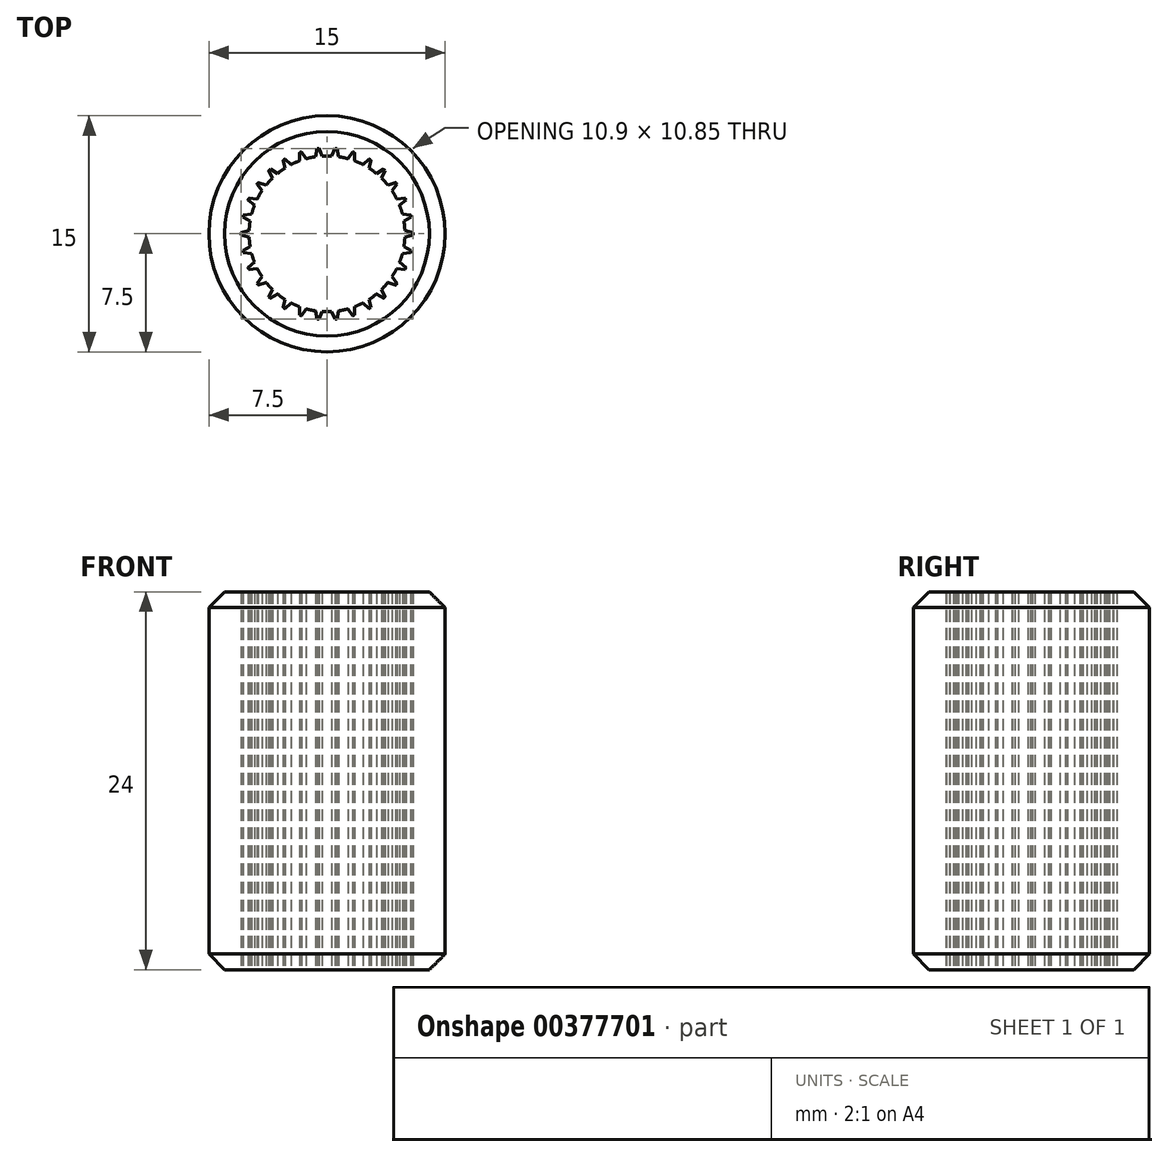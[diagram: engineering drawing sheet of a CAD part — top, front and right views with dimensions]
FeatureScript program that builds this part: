
annotation { "Feature Type Name" : "Feature", "Feature Type Description" : "" }
export const myFeature = defineFeature(function(context is Context, id is Id, definition is map)
    precondition{}
    {
        {
            var Q0;
            Q0=qCreatedBy(makeId("Top.planeOp"),FACE);
            var sketch = newSketch(context, id + "F0", { "sketchPlane" : qUnion([Q0])});
            skCircle(sketch, "E0", {"center": v(0, 0) * mm, "radius": 4.95 * mm, "construction": true});
            skCircle(sketch, "E1", {"center": v(0, 0) * mm, "radius": 7.5 * mm});
            skCircle(sketch, "E2.0", {"center": v(0, 0) * mm, "radius": 5.45 * mm});
            skLineSegment(sketch, "E3", {"start": v(0, 0) * mm, "end": v(0, 9.5) * mm, "construction": true});
            skLineSegment(sketch, "E4", {"start": v(0.5, 5.43) * mm, "end": v(0.3, 4.94) * mm});
            skArc(sketch, "E5", {"start": v(0.3, 4.94) * mm, "mid": v(0.15, 4.95) * mm, "end": v(0, 4.95) * mm});
            skLineSegment(sketch, "E6.MirrorCS", {"start": v(-0.5, 5.43) * mm, "end": v(-0.3, 4.94) * mm});
            skArc(sketch, "E7.MirrorCS", {"start": v(-0.3, 4.94) * mm, "mid": v(-0.15, 4.95) * mm, "end": v(0, 4.95) * mm});
            skLineSegment(sketch, "E8.1.0", {"start": v(-0.64, 5.41) * mm, "end": v(-0.73, 4.9) * mm});
            skLineSegment(sketch, "E8.1.1", {"start": v(-1.62, 5.2) * mm, "end": v(-1.32, 4.77) * mm});
            skArc(sketch, "E8.1.2", {"start": v(-0.73, 4.9) * mm, "mid": v(-0.88, 4.87) * mm, "end": v(-1.03, 4.84) * mm});
            skArc(sketch, "E8.1.3", {"start": v(-1.32, 4.77) * mm, "mid": v(-1.18, 4.8) * mm, "end": v(-1.03, 4.84) * mm});
            skLineSegment(sketch, "E8.2.0", {"start": v(-1.75, 5.16) * mm, "end": v(-1.74, 4.64) * mm});
            skLineSegment(sketch, "E8.2.1", {"start": v(-2.66, 4.75) * mm, "end": v(-2.28, 4.4) * mm});
            skArc(sketch, "E8.2.2", {"start": v(-1.74, 4.64) * mm, "mid": v(-1.88, 4.58) * mm, "end": v(-2.01, 4.52) * mm});
            skArc(sketch, "E8.2.3", {"start": v(-2.28, 4.4) * mm, "mid": v(-2.15, 4.46) * mm, "end": v(-2.01, 4.52) * mm});
            skLineSegment(sketch, "E8.3.0", {"start": v(-2.79, 4.68) * mm, "end": v(-2.66, 4.17) * mm});
            skLineSegment(sketch, "E8.3.1", {"start": v(-3.6, 4.1) * mm, "end": v(-3.15, 3.82) * mm});
            skArc(sketch, "E8.3.2", {"start": v(-2.66, 4.17) * mm, "mid": v(-2.79, 4.1) * mm, "end": v(-2.9, 4) * mm});
            skArc(sketch, "E8.3.3", {"start": v(-3.15, 3.82) * mm, "mid": v(-3.03, 3.91) * mm, "end": v(-2.9, 4) * mm});
            skLineSegment(sketch, "E8.4.0", {"start": v(-3.7, 4) * mm, "end": v(-3.47, 3.53) * mm});
            skLineSegment(sketch, "E8.4.1", {"start": v(-4.37, 3.26) * mm, "end": v(-3.87, 3.08) * mm});
            skArc(sketch, "E8.4.2", {"start": v(-3.47, 3.53) * mm, "mid": v(-3.58, 3.42) * mm, "end": v(-3.68, 3.31) * mm});
            skArc(sketch, "E8.4.3", {"start": v(-3.87, 3.08) * mm, "mid": v(-3.78, 3.2) * mm, "end": v(-3.68, 3.31) * mm});
            skLineSegment(sketch, "E8.5.0", {"start": v(-4.45, 3.15) * mm, "end": v(-4.13, 2.73) * mm});
            skLineSegment(sketch, "E8.5.1", {"start": v(-4.95, 2.28) * mm, "end": v(-4.43, 2.21) * mm});
            skArc(sketch, "E8.5.2", {"start": v(-4.13, 2.73) * mm, "mid": v(-4.2, 2.6) * mm, "end": v(-4.29, 2.48) * mm});
            skArc(sketch, "E8.5.3", {"start": v(-4.43, 2.21) * mm, "mid": v(-4.36, 2.34) * mm, "end": v(-4.29, 2.48) * mm});
            skLineSegment(sketch, "E8.6.0", {"start": v(-5, 2.15) * mm, "end": v(-4.6, 1.81) * mm});
            skLineSegment(sketch, "E8.6.1", {"start": v(-5.32, 1.2) * mm, "end": v(-4.8, 1.24) * mm});
            skArc(sketch, "E8.6.2", {"start": v(-4.6, 1.81) * mm, "mid": v(-4.66, 1.67) * mm, "end": v(-4.7, 1.53) * mm});
            skArc(sketch, "E8.6.3", {"start": v(-4.8, 1.24) * mm, "mid": v(-4.75, 1.39) * mm, "end": v(-4.7, 1.53) * mm});
            skLineSegment(sketch, "E8.7.0", {"start": v(-5.35, 1.06) * mm, "end": v(-4.88, 0.81) * mm});
            skLineSegment(sketch, "E8.7.1", {"start": v(-5.45, 0.07) * mm, "end": v(-4.95, 0.22) * mm});
            skArc(sketch, "E8.7.2", {"start": v(-4.88, 0.81) * mm, "mid": v(-4.9, 0.67) * mm, "end": v(-4.92, 0.52) * mm});
            skArc(sketch, "E8.7.3", {"start": v(-4.95, 0.22) * mm, "mid": v(-4.94, 0.37) * mm, "end": v(-4.92, 0.52) * mm});
            skLineSegment(sketch, "E8.8.0", {"start": v(-5.45, -0.07) * mm, "end": v(-4.95, -0.22) * mm});
            skLineSegment(sketch, "E8.8.1", {"start": v(-5.35, -1.06) * mm, "end": v(-4.88, -0.81) * mm});
            skArc(sketch, "E8.8.2", {"start": v(-4.95, -0.22) * mm, "mid": v(-4.94, -0.37) * mm, "end": v(-4.92, -0.52) * mm});
            skArc(sketch, "E8.8.3", {"start": v(-4.88, -0.81) * mm, "mid": v(-4.9, -0.67) * mm, "end": v(-4.92, -0.52) * mm});
            skLineSegment(sketch, "E8.9.0", {"start": v(-5.32, -1.2) * mm, "end": v(-4.8, -1.24) * mm});
            skLineSegment(sketch, "E8.9.1", {"start": v(-5, -2.15) * mm, "end": v(-4.6, -1.81) * mm});
            skArc(sketch, "E8.9.2", {"start": v(-4.8, -1.24) * mm, "mid": v(-4.75, -1.39) * mm, "end": v(-4.7, -1.53) * mm});
            skArc(sketch, "E8.9.3", {"start": v(-4.6, -1.81) * mm, "mid": v(-4.66, -1.67) * mm, "end": v(-4.7, -1.53) * mm});
            skLineSegment(sketch, "E8.10.0", {"start": v(-4.95, -2.28) * mm, "end": v(-4.43, -2.21) * mm});
            skLineSegment(sketch, "E8.10.1", {"start": v(-4.45, -3.15) * mm, "end": v(-4.13, -2.73) * mm});
            skArc(sketch, "E8.10.2", {"start": v(-4.43, -2.21) * mm, "mid": v(-4.36, -2.34) * mm, "end": v(-4.29, -2.47) * mm});
            skArc(sketch, "E8.10.3", {"start": v(-4.13, -2.73) * mm, "mid": v(-4.2, -2.6) * mm, "end": v(-4.29, -2.47) * mm});
            skLineSegment(sketch, "E8.11.0", {"start": v(-4.37, -3.26) * mm, "end": v(-3.87, -3.08) * mm});
            skLineSegment(sketch, "E8.11.1", {"start": v(-3.7, -4) * mm, "end": v(-3.47, -3.53) * mm});
            skArc(sketch, "E8.11.2", {"start": v(-3.87, -3.08) * mm, "mid": v(-3.78, -3.2) * mm, "end": v(-3.68, -3.31) * mm});
            skArc(sketch, "E8.11.3", {"start": v(-3.47, -3.53) * mm, "mid": v(-3.58, -3.42) * mm, "end": v(-3.68, -3.31) * mm});
            skLineSegment(sketch, "E8.12.0", {"start": v(-3.6, -4.1) * mm, "end": v(-3.15, -3.82) * mm});
            skLineSegment(sketch, "E8.12.1", {"start": v(-2.79, -4.68) * mm, "end": v(-2.66, -4.17) * mm});
            skArc(sketch, "E8.12.2", {"start": v(-3.15, -3.82) * mm, "mid": v(-3.03, -3.91) * mm, "end": v(-2.9, -4) * mm});
            skArc(sketch, "E8.12.3", {"start": v(-2.66, -4.17) * mm, "mid": v(-2.79, -4.1) * mm, "end": v(-2.9, -4) * mm});
            skLineSegment(sketch, "E8.13.0", {"start": v(-2.66, -4.75) * mm, "end": v(-2.28, -4.4) * mm});
            skLineSegment(sketch, "E8.13.1", {"start": v(-1.75, -5.16) * mm, "end": v(-1.74, -4.64) * mm});
            skArc(sketch, "E8.13.2", {"start": v(-2.28, -4.4) * mm, "mid": v(-2.15, -4.46) * mm, "end": v(-2.01, -4.52) * mm});
            skArc(sketch, "E8.13.3", {"start": v(-1.74, -4.64) * mm, "mid": v(-1.88, -4.58) * mm, "end": v(-2.01, -4.52) * mm});
            skLineSegment(sketch, "E8.14.0", {"start": v(-1.62, -5.2) * mm, "end": v(-1.32, -4.77) * mm});
            skLineSegment(sketch, "E8.14.1", {"start": v(-0.64, -5.41) * mm, "end": v(-0.73, -4.9) * mm});
            skArc(sketch, "E8.14.2", {"start": v(-1.32, -4.77) * mm, "mid": v(-1.18, -4.8) * mm, "end": v(-1.03, -4.84) * mm});
            skArc(sketch, "E8.14.3", {"start": v(-0.73, -4.9) * mm, "mid": v(-0.88, -4.87) * mm, "end": v(-1.03, -4.84) * mm});
            skLineSegment(sketch, "E8.15.0", {"start": v(-0.5, -5.43) * mm, "end": v(-0.3, -4.94) * mm});
            skLineSegment(sketch, "E8.15.1", {"start": v(0.5, -5.43) * mm, "end": v(0.3, -4.94) * mm});
            skArc(sketch, "E8.15.2", {"start": v(-0.3, -4.94) * mm, "mid": v(-0.15, -4.95) * mm, "end": v(0, -4.95) * mm});
            skArc(sketch, "E8.15.3", {"start": v(0.3, -4.94) * mm, "mid": v(0.15, -4.95) * mm, "end": v(0, -4.95) * mm});
            skLineSegment(sketch, "E8.16.0", {"start": v(0.64, -5.41) * mm, "end": v(0.73, -4.9) * mm});
            skLineSegment(sketch, "E8.16.1", {"start": v(1.62, -5.2) * mm, "end": v(1.32, -4.77) * mm});
            skArc(sketch, "E8.16.2", {"start": v(0.73, -4.9) * mm, "mid": v(0.88, -4.87) * mm, "end": v(1.03, -4.84) * mm});
            skArc(sketch, "E8.16.3", {"start": v(1.32, -4.77) * mm, "mid": v(1.18, -4.8) * mm, "end": v(1.03, -4.84) * mm});
            skLineSegment(sketch, "E8.17.0", {"start": v(1.75, -5.16) * mm, "end": v(1.74, -4.64) * mm});
            skLineSegment(sketch, "E8.17.1", {"start": v(2.66, -4.75) * mm, "end": v(2.28, -4.4) * mm});
            skArc(sketch, "E8.17.2", {"start": v(1.74, -4.64) * mm, "mid": v(1.88, -4.58) * mm, "end": v(2.01, -4.52) * mm});
            skArc(sketch, "E8.17.3", {"start": v(2.28, -4.4) * mm, "mid": v(2.15, -4.46) * mm, "end": v(2.01, -4.52) * mm});
            skLineSegment(sketch, "E8.18.0", {"start": v(2.79, -4.68) * mm, "end": v(2.66, -4.17) * mm});
            skLineSegment(sketch, "E8.18.1", {"start": v(3.6, -4.1) * mm, "end": v(3.15, -3.82) * mm});
            skArc(sketch, "E8.18.2", {"start": v(2.66, -4.17) * mm, "mid": v(2.79, -4.1) * mm, "end": v(2.9, -4) * mm});
            skArc(sketch, "E8.18.3", {"start": v(3.15, -3.82) * mm, "mid": v(3.03, -3.91) * mm, "end": v(2.9, -4) * mm});
            skLineSegment(sketch, "E8.19.0", {"start": v(3.7, -4) * mm, "end": v(3.47, -3.53) * mm});
            skLineSegment(sketch, "E8.19.1", {"start": v(4.37, -3.26) * mm, "end": v(3.87, -3.08) * mm});
            skArc(sketch, "E8.19.2", {"start": v(3.47, -3.53) * mm, "mid": v(3.58, -3.42) * mm, "end": v(3.68, -3.31) * mm});
            skArc(sketch, "E8.19.3", {"start": v(3.87, -3.08) * mm, "mid": v(3.78, -3.2) * mm, "end": v(3.68, -3.31) * mm});
            skLineSegment(sketch, "E8.20.0", {"start": v(4.45, -3.15) * mm, "end": v(4.13, -2.73) * mm});
            skLineSegment(sketch, "E8.20.1", {"start": v(4.95, -2.28) * mm, "end": v(4.43, -2.21) * mm});
            skArc(sketch, "E8.20.2", {"start": v(4.13, -2.73) * mm, "mid": v(4.2, -2.6) * mm, "end": v(4.29, -2.48) * mm});
            skArc(sketch, "E8.20.3", {"start": v(4.43, -2.21) * mm, "mid": v(4.36, -2.34) * mm, "end": v(4.29, -2.48) * mm});
            skLineSegment(sketch, "E8.21.0", {"start": v(5, -2.15) * mm, "end": v(4.6, -1.81) * mm});
            skLineSegment(sketch, "E8.21.1", {"start": v(5.32, -1.2) * mm, "end": v(4.8, -1.24) * mm});
            skArc(sketch, "E8.21.2", {"start": v(4.6, -1.81) * mm, "mid": v(4.66, -1.67) * mm, "end": v(4.7, -1.53) * mm});
            skArc(sketch, "E8.21.3", {"start": v(4.8, -1.24) * mm, "mid": v(4.75, -1.39) * mm, "end": v(4.7, -1.53) * mm});
            skLineSegment(sketch, "E8.22.0", {"start": v(5.35, -1.06) * mm, "end": v(4.88, -0.81) * mm});
            skLineSegment(sketch, "E8.22.1", {"start": v(5.45, -0.07) * mm, "end": v(4.95, -0.22) * mm});
            skArc(sketch, "E8.22.2", {"start": v(4.88, -0.81) * mm, "mid": v(4.9, -0.67) * mm, "end": v(4.92, -0.52) * mm});
            skArc(sketch, "E8.22.3", {"start": v(4.95, -0.22) * mm, "mid": v(4.94, -0.37) * mm, "end": v(4.92, -0.52) * mm});
            skLineSegment(sketch, "E8.23.0", {"start": v(5.45, 0.07) * mm, "end": v(4.95, 0.22) * mm});
            skLineSegment(sketch, "E8.23.1", {"start": v(5.35, 1.06) * mm, "end": v(4.88, 0.81) * mm});
            skArc(sketch, "E8.23.2", {"start": v(4.95, 0.22) * mm, "mid": v(4.94, 0.37) * mm, "end": v(4.92, 0.52) * mm});
            skArc(sketch, "E8.23.3", {"start": v(4.88, 0.81) * mm, "mid": v(4.9, 0.67) * mm, "end": v(4.92, 0.52) * mm});
            skLineSegment(sketch, "E8.24.0", {"start": v(5.32, 1.2) * mm, "end": v(4.8, 1.24) * mm});
            skLineSegment(sketch, "E8.24.1", {"start": v(5, 2.15) * mm, "end": v(4.6, 1.81) * mm});
            skArc(sketch, "E8.24.2", {"start": v(4.8, 1.24) * mm, "mid": v(4.75, 1.39) * mm, "end": v(4.7, 1.53) * mm});
            skArc(sketch, "E8.24.3", {"start": v(4.6, 1.81) * mm, "mid": v(4.66, 1.67) * mm, "end": v(4.7, 1.53) * mm});
            skLineSegment(sketch, "E8.25.0", {"start": v(4.95, 2.28) * mm, "end": v(4.43, 2.21) * mm});
            skLineSegment(sketch, "E8.25.1", {"start": v(4.45, 3.15) * mm, "end": v(4.13, 2.73) * mm});
            skArc(sketch, "E8.25.2", {"start": v(4.43, 2.21) * mm, "mid": v(4.36, 2.34) * mm, "end": v(4.29, 2.47) * mm});
            skArc(sketch, "E8.25.3", {"start": v(4.13, 2.73) * mm, "mid": v(4.2, 2.6) * mm, "end": v(4.29, 2.47) * mm});
            skLineSegment(sketch, "E8.26.0", {"start": v(4.37, 3.26) * mm, "end": v(3.87, 3.08) * mm});
            skLineSegment(sketch, "E8.26.1", {"start": v(3.7, 4) * mm, "end": v(3.47, 3.53) * mm});
            skArc(sketch, "E8.26.2", {"start": v(3.87, 3.08) * mm, "mid": v(3.78, 3.2) * mm, "end": v(3.68, 3.31) * mm});
            skArc(sketch, "E8.26.3", {"start": v(3.47, 3.53) * mm, "mid": v(3.58, 3.42) * mm, "end": v(3.68, 3.31) * mm});
            skLineSegment(sketch, "E8.27.0", {"start": v(3.6, 4.1) * mm, "end": v(3.15, 3.82) * mm});
            skLineSegment(sketch, "E8.27.1", {"start": v(2.79, 4.68) * mm, "end": v(2.66, 4.17) * mm});
            skArc(sketch, "E8.27.2", {"start": v(3.15, 3.82) * mm, "mid": v(3.03, 3.91) * mm, "end": v(2.9, 4) * mm});
            skArc(sketch, "E8.27.3", {"start": v(2.66, 4.17) * mm, "mid": v(2.79, 4.1) * mm, "end": v(2.9, 4) * mm});
            skLineSegment(sketch, "E8.28.0", {"start": v(2.66, 4.75) * mm, "end": v(2.28, 4.4) * mm});
            skLineSegment(sketch, "E8.28.1", {"start": v(1.75, 5.16) * mm, "end": v(1.74, 4.64) * mm});
            skArc(sketch, "E8.28.2", {"start": v(2.28, 4.4) * mm, "mid": v(2.15, 4.46) * mm, "end": v(2.01, 4.52) * mm});
            skArc(sketch, "E8.28.3", {"start": v(1.74, 4.64) * mm, "mid": v(1.88, 4.58) * mm, "end": v(2.01, 4.52) * mm});
            skLineSegment(sketch, "E8.29.0", {"start": v(1.62, 5.2) * mm, "end": v(1.32, 4.77) * mm});
            skLineSegment(sketch, "E8.29.1", {"start": v(0.64, 5.41) * mm, "end": v(0.73, 4.9) * mm});
            skArc(sketch, "E8.29.2", {"start": v(1.32, 4.77) * mm, "mid": v(1.18, 4.8) * mm, "end": v(1.03, 4.84) * mm});
            skArc(sketch, "E8.29.3", {"start": v(0.73, 4.9) * mm, "mid": v(0.88, 4.87) * mm, "end": v(1.03, 4.84) * mm});
            skSolve(sketch);
        }
        {
            var Q0;
            {var subQ0=sQuery(id+"F0.wireOp",EDGE,"E8.4.0");Q0=makeQuery(id+"F0.imprint","IMPRINT",FACE,{"disambiguationData":[TD([[makeQuery(id+"F0.imprint","IMPRINT",EDGE,{"derivedFrom":subQ0}),-1.0]])]});}
            var Q1;
            {var subQ1=sQuery(id+"F0.wireOp",EDGE,"E8.5.0");Q1=makeQuery(id+"F0.imprint","IMPRINT",FACE,{"disambiguationData":[TD([[makeQuery(id+"F0.imprint","IMPRINT",EDGE,{"derivedFrom":subQ1}),-1.0]])]});}
            var Q2;
            {var subQ1=sQuery(id+"F0.wireOp",EDGE,"E8.3.0");Q2=makeQuery(id+"F0.imprint","IMPRINT",FACE,{"disambiguationData":[TD([[makeQuery(id+"F0.imprint","IMPRINT",EDGE,{"derivedFrom":subQ1}),-1.0]])]});}
            var Q3;
            {var subQ1=sQuery(id+"F0.wireOp",EDGE,"E8.2.0");Q3=makeQuery(id+"F0.imprint","IMPRINT",FACE,{"disambiguationData":[TD([[makeQuery(id+"F0.imprint","IMPRINT",EDGE,{"derivedFrom":subQ1}),-1.0]])]});}
            var Q4;
            {var subQ1=sQuery(id+"F0.wireOp",EDGE,"E8.1.0");Q4=makeQuery(id+"F0.imprint","IMPRINT",FACE,{"disambiguationData":[TD([[makeQuery(id+"F0.imprint","IMPRINT",EDGE,{"derivedFrom":subQ1}),-1.0]])]});}
            var Q5;
            {var subQ1=sQuery(id+"F0.wireOp",EDGE,"E4");Q5=makeQuery(id+"F0.imprint","IMPRINT",FACE,{"disambiguationData":[TD([[makeQuery(id+"F0.imprint","IMPRINT",EDGE,{"derivedFrom":subQ1}),-1.0]])]});}
            var Q6;
            {var subQ0=sQuery(id+"F0.wireOp",EDGE,"E8.29.0");Q6=makeQuery(id+"F0.imprint","IMPRINT",FACE,{"disambiguationData":[TD([[makeQuery(id+"F0.imprint","IMPRINT",EDGE,{"derivedFrom":subQ0}),-1.0]])]});}
            var Q7;
            Q7=makeQuery(id+"F0.imprint","IMPRINT",FACE,{"disambiguationData":[TD([[makeQuery(id+"F0.imprint","IMPRINT",EDGE,{"derivedFrom":sQuery(id+"F0.wireOp",EDGE,"E1")}),1.0]])]});
            var Q8;
            {var subQ1=sQuery(id+"F0.wireOp",EDGE,"E8.28.0");Q8=makeQuery(id+"F0.imprint","IMPRINT",FACE,{"disambiguationData":[TD([[makeQuery(id+"F0.imprint","IMPRINT",EDGE,{"derivedFrom":subQ1}),-1.0]])]});}
            var Q9;
            {var subQ1=sQuery(id+"F0.wireOp",EDGE,"E8.27.0");Q9=makeQuery(id+"F0.imprint","IMPRINT",FACE,{"disambiguationData":[TD([[makeQuery(id+"F0.imprint","IMPRINT",EDGE,{"derivedFrom":subQ1}),-1.0]])]});}
            var Q10;
            {var subQ1=sQuery(id+"F0.wireOp",EDGE,"E8.26.0");Q10=makeQuery(id+"F0.imprint","IMPRINT",FACE,{"disambiguationData":[TD([[makeQuery(id+"F0.imprint","IMPRINT",EDGE,{"derivedFrom":subQ1}),-1.0]])]});}
            var Q11;
            {var subQ1=sQuery(id+"F0.wireOp",EDGE,"E8.25.0");Q11=makeQuery(id+"F0.imprint","IMPRINT",FACE,{"disambiguationData":[TD([[makeQuery(id+"F0.imprint","IMPRINT",EDGE,{"derivedFrom":subQ1}),-1.0]])]});}
            var Q12;
            {var subQ0=sQuery(id+"F0.wireOp",EDGE,"E8.24.0");Q12=makeQuery(id+"F0.imprint","IMPRINT",FACE,{"disambiguationData":[TD([[makeQuery(id+"F0.imprint","IMPRINT",EDGE,{"derivedFrom":subQ0}),-1.0]])]});}
            var Q13;
            {var subQ0=sQuery(id+"F0.wireOp",EDGE,"E8.23.0");Q13=makeQuery(id+"F0.imprint","IMPRINT",FACE,{"disambiguationData":[TD([[makeQuery(id+"F0.imprint","IMPRINT",EDGE,{"derivedFrom":subQ0}),-1.0]])]});}
            var Q14;
            {var subQ1=sQuery(id+"F0.wireOp",EDGE,"E8.6.0");Q14=makeQuery(id+"F0.imprint","IMPRINT",FACE,{"disambiguationData":[TD([[makeQuery(id+"F0.imprint","IMPRINT",EDGE,{"derivedFrom":subQ1}),-1.0]])]});}
            var Q15;
            {var subQ1=sQuery(id+"F0.wireOp",EDGE,"E8.7.0");Q15=makeQuery(id+"F0.imprint","IMPRINT",FACE,{"disambiguationData":[TD([[makeQuery(id+"F0.imprint","IMPRINT",EDGE,{"derivedFrom":subQ1}),-1.0]])]});}
            var Q16;
            {var subQ1=sQuery(id+"F0.wireOp",EDGE,"E8.8.0");Q16=makeQuery(id+"F0.imprint","IMPRINT",FACE,{"disambiguationData":[TD([[makeQuery(id+"F0.imprint","IMPRINT",EDGE,{"derivedFrom":subQ1}),-1.0]])]});}
            var Q17;
            {var subQ0=sQuery(id+"F0.wireOp",EDGE,"E8.9.0");Q17=makeQuery(id+"F0.imprint","IMPRINT",FACE,{"disambiguationData":[TD([[makeQuery(id+"F0.imprint","IMPRINT",EDGE,{"derivedFrom":subQ0}),-1.0]])]});}
            var Q18;
            {var subQ1=sQuery(id+"F0.wireOp",EDGE,"E8.10.0");Q18=makeQuery(id+"F0.imprint","IMPRINT",FACE,{"disambiguationData":[TD([[makeQuery(id+"F0.imprint","IMPRINT",EDGE,{"derivedFrom":subQ1}),-1.0]])]});}
            var Q19;
            {var subQ1=sQuery(id+"F0.wireOp",EDGE,"E8.11.0");Q19=makeQuery(id+"F0.imprint","IMPRINT",FACE,{"disambiguationData":[TD([[makeQuery(id+"F0.imprint","IMPRINT",EDGE,{"derivedFrom":subQ1}),-1.0]])]});}
            var Q20;
            {var subQ1=sQuery(id+"F0.wireOp",EDGE,"E8.12.0");Q20=makeQuery(id+"F0.imprint","IMPRINT",FACE,{"disambiguationData":[TD([[makeQuery(id+"F0.imprint","IMPRINT",EDGE,{"derivedFrom":subQ1}),-1.0]])]});}
            var Q21;
            {var subQ1=sQuery(id+"F0.wireOp",EDGE,"E8.13.0");Q21=makeQuery(id+"F0.imprint","IMPRINT",FACE,{"disambiguationData":[TD([[makeQuery(id+"F0.imprint","IMPRINT",EDGE,{"derivedFrom":subQ1}),-1.0]])]});}
            var Q22;
            {var subQ0=sQuery(id+"F0.wireOp",EDGE,"E8.14.0");Q22=makeQuery(id+"F0.imprint","IMPRINT",FACE,{"disambiguationData":[TD([[makeQuery(id+"F0.imprint","IMPRINT",EDGE,{"derivedFrom":subQ0}),-1.0]])]});}
            var Q23;
            {var subQ1=sQuery(id+"F0.wireOp",EDGE,"E8.15.0");Q23=makeQuery(id+"F0.imprint","IMPRINT",FACE,{"disambiguationData":[TD([[makeQuery(id+"F0.imprint","IMPRINT",EDGE,{"derivedFrom":subQ1}),-1.0]])]});}
            var Q24;
            {var subQ1=sQuery(id+"F0.wireOp",EDGE,"E8.16.0");Q24=makeQuery(id+"F0.imprint","IMPRINT",FACE,{"disambiguationData":[TD([[makeQuery(id+"F0.imprint","IMPRINT",EDGE,{"derivedFrom":subQ1}),-1.0]])]});}
            var Q25;
            {var subQ1=sQuery(id+"F0.wireOp",EDGE,"E8.17.0");Q25=makeQuery(id+"F0.imprint","IMPRINT",FACE,{"disambiguationData":[TD([[makeQuery(id+"F0.imprint","IMPRINT",EDGE,{"derivedFrom":subQ1}),-1.0]])]});}
            var Q26;
            {var subQ1=sQuery(id+"F0.wireOp",EDGE,"E8.18.0");Q26=makeQuery(id+"F0.imprint","IMPRINT",FACE,{"disambiguationData":[TD([[makeQuery(id+"F0.imprint","IMPRINT",EDGE,{"derivedFrom":subQ1}),-1.0]])]});}
            var Q27;
            {var subQ0=sQuery(id+"F0.wireOp",EDGE,"E8.19.0");Q27=makeQuery(id+"F0.imprint","IMPRINT",FACE,{"disambiguationData":[TD([[makeQuery(id+"F0.imprint","IMPRINT",EDGE,{"derivedFrom":subQ0}),-1.0]])]});}
            var Q28;
            {var subQ0=sQuery(id+"F0.wireOp",EDGE,"E8.20.0");Q28=makeQuery(id+"F0.imprint","IMPRINT",FACE,{"disambiguationData":[TD([[makeQuery(id+"F0.imprint","IMPRINT",EDGE,{"derivedFrom":subQ0}),-1.0]])]});}
            var Q29;
            {var subQ1=sQuery(id+"F0.wireOp",EDGE,"E8.21.0");Q29=makeQuery(id+"F0.imprint","IMPRINT",FACE,{"disambiguationData":[TD([[makeQuery(id+"F0.imprint","IMPRINT",EDGE,{"derivedFrom":subQ1}),-1.0]])]});}
            var Q30;
            {var subQ1=sQuery(id+"F0.wireOp",EDGE,"E8.22.0");Q30=makeQuery(id+"F0.imprint","IMPRINT",FACE,{"disambiguationData":[TD([[makeQuery(id+"F0.imprint","IMPRINT",EDGE,{"derivedFrom":subQ1}),-1.0]])]});}
            extrude(context, id + "F1", {"entities" : qUnion([Q0, Q1, Q2, Q3, Q4, Q5, Q6, Q7, Q8, Q9, Q10, Q11, Q12, Q13, Q14, Q15, Q16, Q17, Q18, Q19, Q20, Q21, Q22, Q23, Q24, Q25, Q26, Q27, Q28, Q29, Q30]), "depth" : 24 * mm});
        }
        {
            var Q0;
            Q0=makeQuery(id+"F1.opExtrude","CAP_EDGE",EDGE,{"disambiguationData":[OSD([sQuery(id+"F0.wireOp",EDGE,"E1")])],"isStart":true});
            var Q1;
            Q1=makeQuery(id+"F1.opExtrude","CAP_EDGE",EDGE,{"disambiguationData":[OSD([sQuery(id+"F0.wireOp",EDGE,"E1")])],"isStart":false});
            chamfer(context, id + "F2", {"entities" : qUnion([Q0, Q1]), "width" : 1 * mm, "tangentPropagation" : true});
        }
    });
